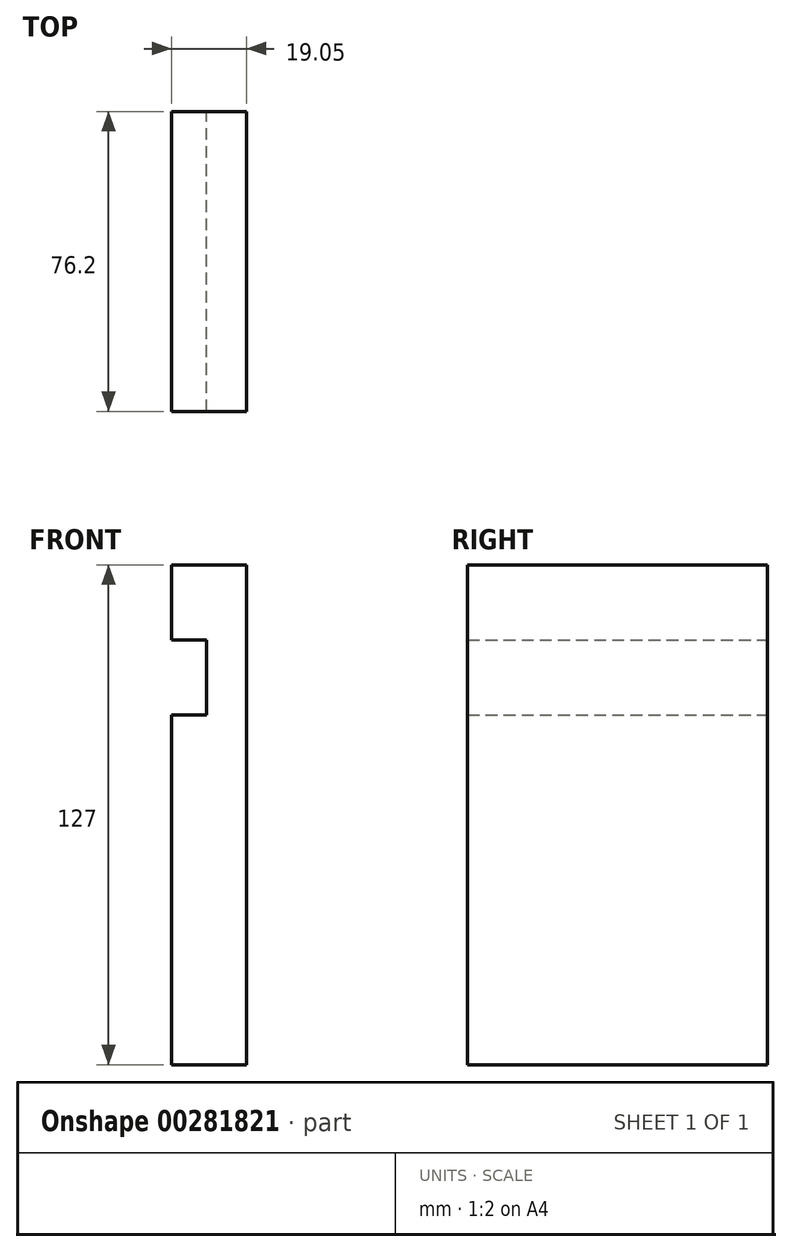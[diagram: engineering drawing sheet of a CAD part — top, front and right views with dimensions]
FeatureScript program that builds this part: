
annotation { "Feature Type Name" : "Feature", "Feature Type Description" : "" }
export const myFeature = defineFeature(function(context is Context, id is Id, definition is map)
    precondition{}
    {
        {
            var Q0;
            Q0=qCreatedBy(makeId("Front.planeOp"),FACE);
            var sketch = newSketch(context, id + "F0", { "sketchPlane" : qUnion([Q0])});
            skLineSegment(sketch, "E0", {"start": v(0, 0) * mm, "end": v(0, 127) * mm});
            skLineSegment(sketch, "E1", {"start": v(0, 127) * mm, "end": v(-19.05, 127) * mm});
            skLineSegment(sketch, "E2", {"start": v(-19.05, 127) * mm, "end": v(-19.05, 107.95) * mm});
            skLineSegment(sketch, "E3", {"start": v(-19.05, 107.95) * mm, "end": v(-10.16, 107.95) * mm});
            skLineSegment(sketch, "E4", {"start": v(-10.16, 107.95) * mm, "end": v(-10.16, 88.9) * mm});
            skLineSegment(sketch, "E5", {"start": v(-10.16, 88.9) * mm, "end": v(-19.05, 88.9) * mm});
            skLineSegment(sketch, "E6", {"start": v(-19.05, 88.9) * mm, "end": v(-19.05, 0) * mm});
            skLineSegment(sketch, "E7", {"start": v(-19.05, 0) * mm, "end": v(0, 0) * mm});
            skSolve(sketch);
        }
        {
            var Q0;
            Q0 = qSketchRegion(id + "F0", true);
            extrude(context, id + "F1", {"entities" : qUnion([Q0]), "depth" : 76.2 * mm});
        }
    });
